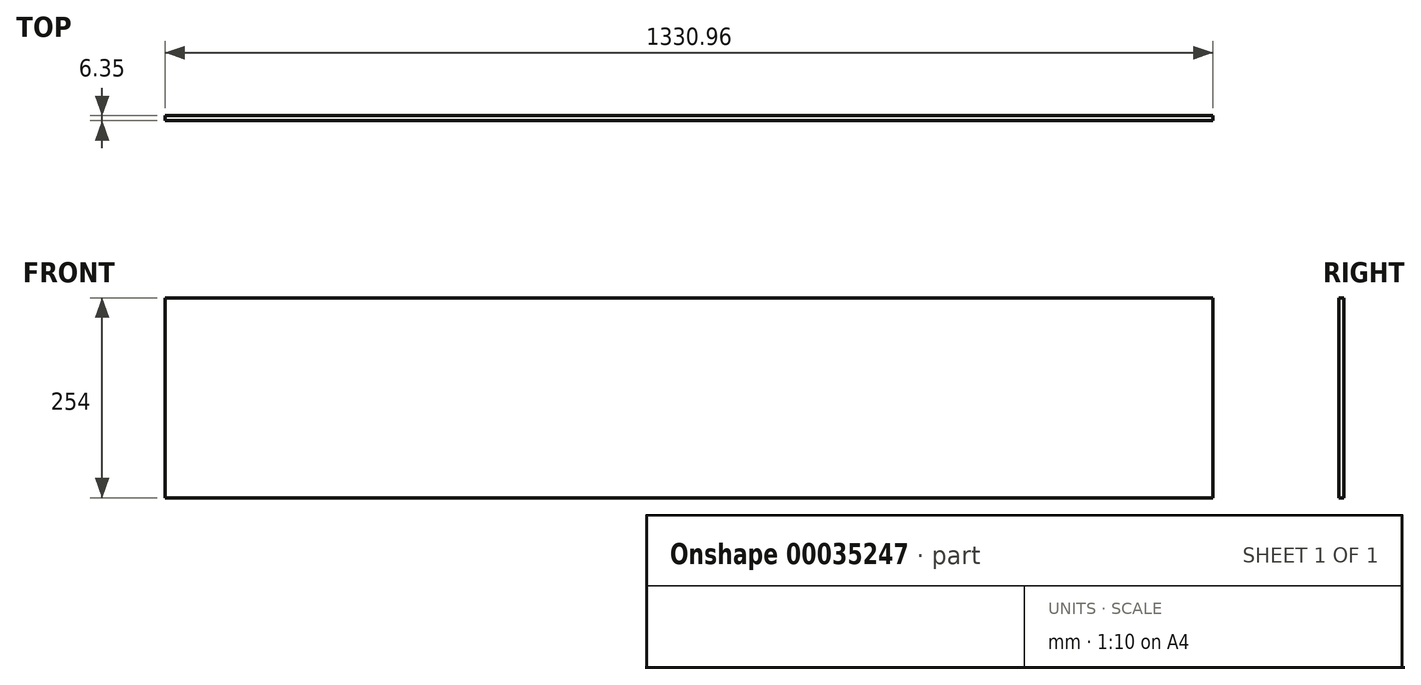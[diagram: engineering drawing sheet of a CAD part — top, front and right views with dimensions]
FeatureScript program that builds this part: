
annotation { "Feature Type Name" : "Feature", "Feature Type Description" : "" }
export const myFeature = defineFeature(function(context is Context, id is Id, definition is map)
    precondition{}
    {
        {
            var Q0;
            Q0=qCreatedBy(makeId("Front.planeOp"),FACE);
            var sketch = newSketch(context, id + "F0", { "sketchPlane" : qUnion([Q0])});
            skLineSegment(sketch, "E0.rect.bottom", {"start": v(665.48, -127) * mm, "end": v(-665.48, -127) * mm});
            skLineSegment(sketch, "E0.rect.top", {"start": v(665.48, 127) * mm, "end": v(-665.48, 127) * mm});
            skLineSegment(sketch, "E0.rect.left", {"start": v(665.48, -127) * mm, "end": v(665.48, 127) * mm});
            skLineSegment(sketch, "E0.rect.right", {"start": v(-665.48, -127) * mm, "end": v(-665.48, 127) * mm});
            skPoint(sketch, "E0.rect.middle", {"position": v(0, 0) * mm});
            skSolve(sketch);
        }
        {
            var Q0;
            Q0=makeQuery(id+"F0.imprint","IMPRINT",FACE,{"disambiguationData":[TD([[makeQuery(id+"F0.imprint","IMPRINT",EDGE,{"derivedFrom":sQuery(id+"F0.wireOp",EDGE,"E0.rect.bottom")}),-1.0]])]});
            extrude(context, id + "F1", {"entities" : qUnion([Q0]), "depth" : 6.35 * mm});
        }
    });
